# Revit family: Shower-Handshower_Kit-KOHLER-Purist-K-22178_1
name_source: partatom
category: Plumbing Fixtures
revit_build: Autodesk Revit 2015 (Build: 20140606_1530(x64)
units: mm (PartAtom-declared; Revit-internal decimal feet)

## types (4) — shared parameters
ADA Compliant = Yes
Assembly Code = D2010700
CW Connection = No
Cold Water Inlet = Cold Water Inlet
Date Modified = 04/23/2019
Default Elevation = 42"
Drain Included = No
HW Connection = Yes
Height = 28"
Hot Water Inlet = Tempered Water Inlet
Length = 5 5/8"
Manufacturer = KOHLER Co.
MasterFormat 1995 = 15410
MasterFormat 2004 = 22.41.23
Material = Premium Metal Construction
Panel Thickness = 0"
Pressure = 45.00 psi
Product Documentation Link = https://www.us.kohler.com
Product Name = Purist
Product Page URL = http://www.us.kohler.com
URL = https://www.us.kohler.com
Vent Connection = No
Waste Connection = No
Waste Water Outlet = Waste Water Outlet
Width = 6 9/32"

## per-type parameters (varying)
| type | Description | Finish | Flow Rate | Model | Type | WaterSense Certified |
| 2.5 GPM, CP-Polished Chrome | 2.5 gpm multifunction handshower kit with Katalyst air-induction technology | Kohler-Metal-CP-Polished_Chrome | 3 GPM | K-22178-CP | 1 | No |
| 2.5 GPM, BN-Vibrant Brushed Nickel | 2.5 gpm multifunction handshower kit with Katalyst air-induction technology | Kohler-Metal-BN-Vibrant_Brushed_Nickel | 3 GPM | K-22178-BN | 2 | No |
| 1.75 GPM, CP-Polished Chrome | 1.75 gpm multifunction handshower kit with Katalyst air-induction technology | Kohler-Metal-CP-Polished_Chrome | 2 GPM | K-22178-G-CP | 3 | Yes |
| 1.75 GPM, BN-Vibrant Brushed Nickel | 1.75 gpm multifunction handshower kit with Katalyst air-induction technology | Kohler-Metal-BN-Vibrant_Brushed_Nickel | 2 GPM | K-22178-G-BN | 4 | Yes |

## geometry (parser evidence)
native form markers: Sweep x6
no freeform markers — native parametric forms only
